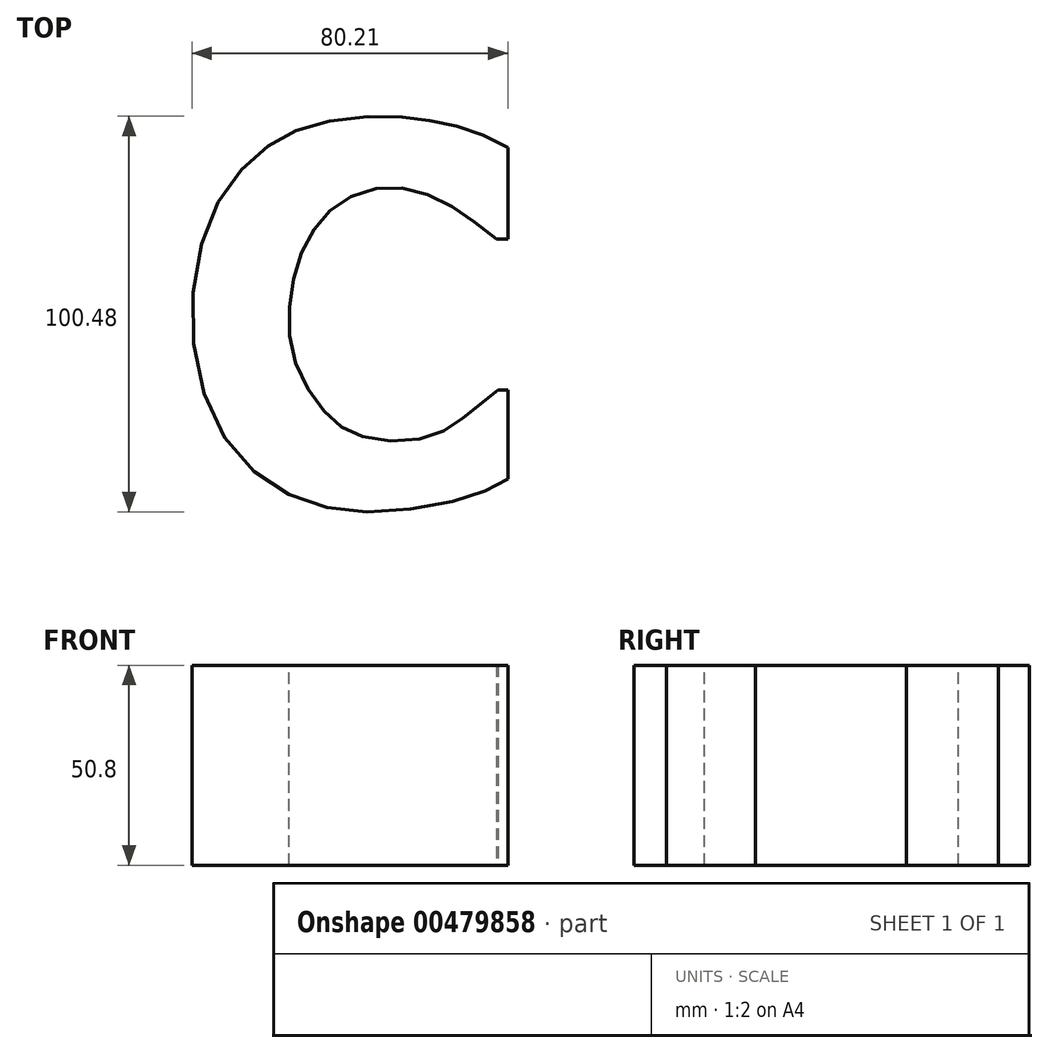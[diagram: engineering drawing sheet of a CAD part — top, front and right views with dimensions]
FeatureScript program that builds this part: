
annotation { "Feature Type Name" : "Feature", "Feature Type Description" : "" }
export const myFeature = defineFeature(function(context is Context, id is Id, definition is map)
    precondition{}
    {
        {
            var Q0;
            Q0=qCreatedBy(makeId("Top.planeOp"),FACE);
            var sketch = newSketch(context, id + "F0", { "sketchPlane" : qUnion([Q0])});
            skFitSpline(sketch, "E0", {"points": [v(12.6, 20.15) * mm, v(0, 29.25) * mm, v(-13.75, 33.32) * mm, v(-26.73, 29.64) * mm, v(-35.26, 20.15) * mm, v(-39.71, 5.42) * mm, v(-38.55, -10.85) * mm, v(-30.6, -24.22) * mm, v(-21.31, -30.03) * mm, v(-5.04, -30.22) * mm, v(5.04, -24.6) * mm, v(12.98, -18.21) * mm], "startDerivative": vector(-125.93, 102.9) * mm, "endDerivative": vector(100.12, 81.95) * mm});
            skLineSegment(sketch, "E1", {"start": v(12.98, -18.21) * mm, "end": v(15.5, -18.21) * mm});
            skLineSegment(sketch, "E2", {"start": v(15.5, -18.21) * mm, "end": v(15.5, -40.85) * mm});
            skLineSegment(sketch, "E3", {"start": v(12.6, 20.15) * mm, "end": v(15.5, 20.15) * mm});
            skLineSegment(sketch, "E4", {"start": v(15.5, 20.15) * mm, "end": v(15.5, 43.45) * mm});
            skPoint(sketch, "E5.7.internal.snap0", {"position": v(-64.7, 1.16) * mm});
            skFitSpline(sketch, "E5", {"points": [v(15.5, 43.45) * mm, v(6.3, 47.77) * mm, v(-3.85, 50.2) * mm, v(-14.44, 51.34) * mm, v(-33.1, 49.5) * mm, v(-45.78, 43.45) * mm, v(-58.2, 29.3) * mm, v(-64.7, 0) * mm, v(-55.91, -31.15) * mm, v(-37.03, -46.07) * mm, v(-15.77, -49.02) * mm, v(6.71, -45.01) * mm, v(15.5, -40.85) * mm], "startDerivative": vector(-142.37, 75.98) * mm, "endDerivative": vector(122.16, 70.15) * mm});
            skSolve(sketch);
        }
        {
            var Q0;
            Q0=makeQuery(id+"F0.imprint","IMPRINT",FACE,{"disambiguationData":[TD([[makeQuery(id+"F0.imprint","IMPRINT",EDGE,{"derivedFrom":sQuery(id+"F0.wireOp",EDGE,"E0")}),-1.0]])]});
            extrude(context, id + "F1", {"entities" : qUnion([Q0]), "depth" : 50.8 * mm});
        }
    });
